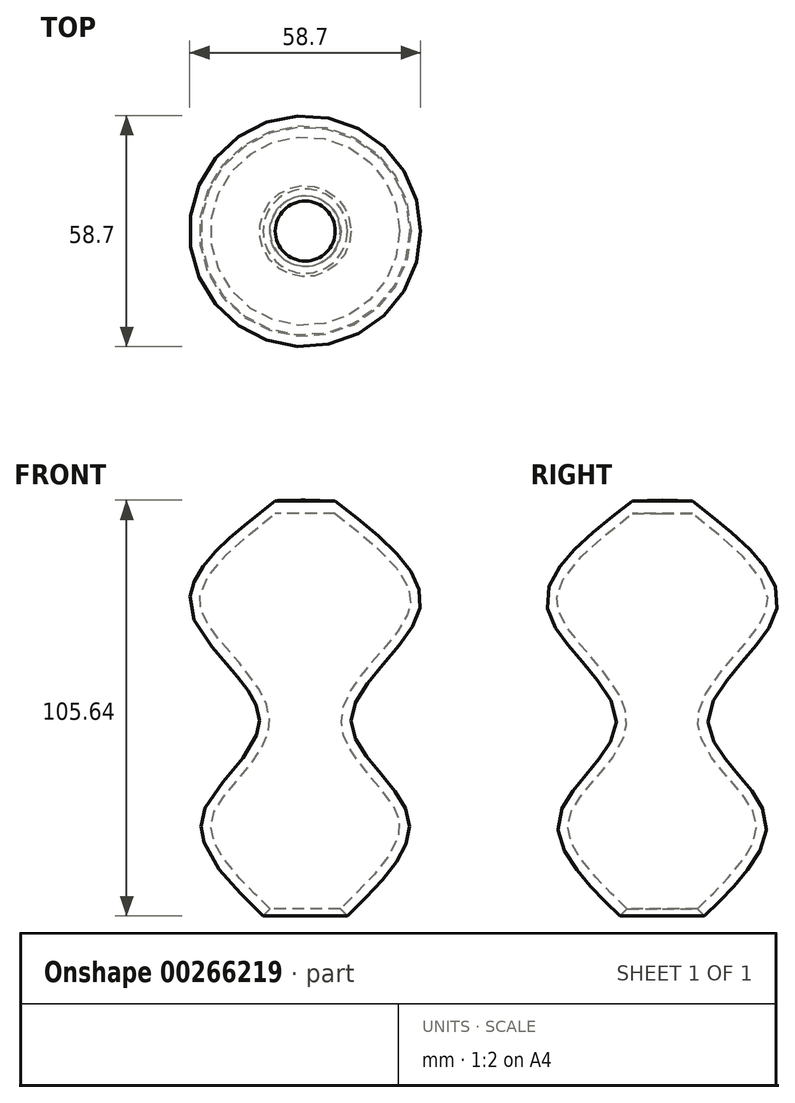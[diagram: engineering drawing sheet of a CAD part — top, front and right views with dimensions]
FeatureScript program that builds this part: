
annotation { "Feature Type Name" : "Feature", "Feature Type Description" : "" }
export const myFeature = defineFeature(function(context is Context, id is Id, definition is map)
    precondition{}
    {
        {
            var Q0;
            Q0=qCreatedBy(makeId("Front.planeOp"),FACE);
            var sketch = newSketch(context, id + "F0", { "sketchPlane" : qUnion([Q0])});
            skLineSegment(sketch, "E0", {"start": v(0, 55.86) * mm, "end": v(0, -49.4) * mm});
            skFitSpline(sketch, "E1", {"points": [v(7.62, 55.7) * mm, v(29.13, 28.2) * mm, v(11.61, 0) * mm, v(26.18, -24.33) * mm, v(10.7, -49.78) * mm], "startDerivative": vector(129.88, -103.32) * mm, "endDerivative": vector(-108.77, -105.55) * mm});
            skLineSegment(sketch, "E2", {"start": v(0, 55.86) * mm, "end": v(7.62, 55.7) * mm});
            skFitSpline(sketch, "E3.0", {"points": [v(6.04, 53.7) * mm, v(7.4, 52.63) * mm, v(10.12, 50.48) * mm, v(14.08, 47.3) * mm, v(17.77, 44.14) * mm, v(21.01, 41.03) * mm, v(23.67, 37.99) * mm, v(25.6, 35.05) * mm, v(26.5, 32.77) * mm, v(26.8, 31.05) * mm, v(26.82, 30) * mm, v(26.73, 29.16) * mm, v(26.6, 28.52) * mm, v(26.42, 27.86) * mm, v(26.1, 26.94) * mm, v(25.53, 25.72) * mm, v(24.32, 23.67) * mm, v(22.31, 20.95) * mm, v(19.43, 17.55) * mm, v(16.37, 14.05) * mm, v(13.94, 11.07) * mm, v(12.21, 8.62) * mm, v(11.07, 6.74) * mm, v(10.12, 4.8) * mm, v(9.53, 3.11) * mm, v(9.23, 1.71) * mm, v(9.09, 0.65) * mm, v(9.06, -0.44) * mm, v(9.13, -1.51) * mm, v(9.3, -2.56) * mm, v(9.64, -3.92) * mm, v(10.25, -5.55) * mm, v(11.2, -7.4) * mm, v(12.7, -9.76) * mm, v(14.89, -12.56) * mm, v(17.66, -15.78) * mm, v(19.83, -18.35) * mm, v(21.33, -20.34) * mm, v(22.3, -21.78) * mm, v(23.06, -23.16) * mm, v(23.6, -24.46) * mm, v(23.9, -25.65) * mm, v(24, -26.85) * mm, v(23.93, -28.1) * mm, v(23.57, -29.82) * mm, v(22.66, -32.14) * mm, v(20.84, -35.12) * mm, v(18.41, -38.23) * mm, v(15.52, -41.42) * mm, v(12.31, -44.66) * mm, v(10.06, -46.85) * mm, v(8.92, -47.95) * mm]});
            skLineSegment(sketch, "E4", {"start": v(8.92, -47.95) * mm, "end": v(10.7, -49.78) * mm});
            skLineSegment(sketch, "E5", {"start": v(7.62, 52.45) * mm, "end": v(0, 52.45) * mm});
            skSolve(sketch);
        }
        {
            var Q0;
            Q0=makeQuery(id+"F0.imprint","IMPRINT",FACE,{"disambiguationData":[TD([[makeQuery(id+"F0.imprint","IMPRINT",EDGE,{"derivedFrom":sQuery(id+"F0.wireOp",EDGE,"E1")}),-1.0]])]});
            var Q1;
            Q1=sQuery(id+"F0.wireOp",EDGE,"E0");
            revolve(context, id + "F1", {"entities" : qUnion([Q0]), "axis" : qUnion([Q1]), "revolveType" : RevolveType.FULL});
        }
    });
